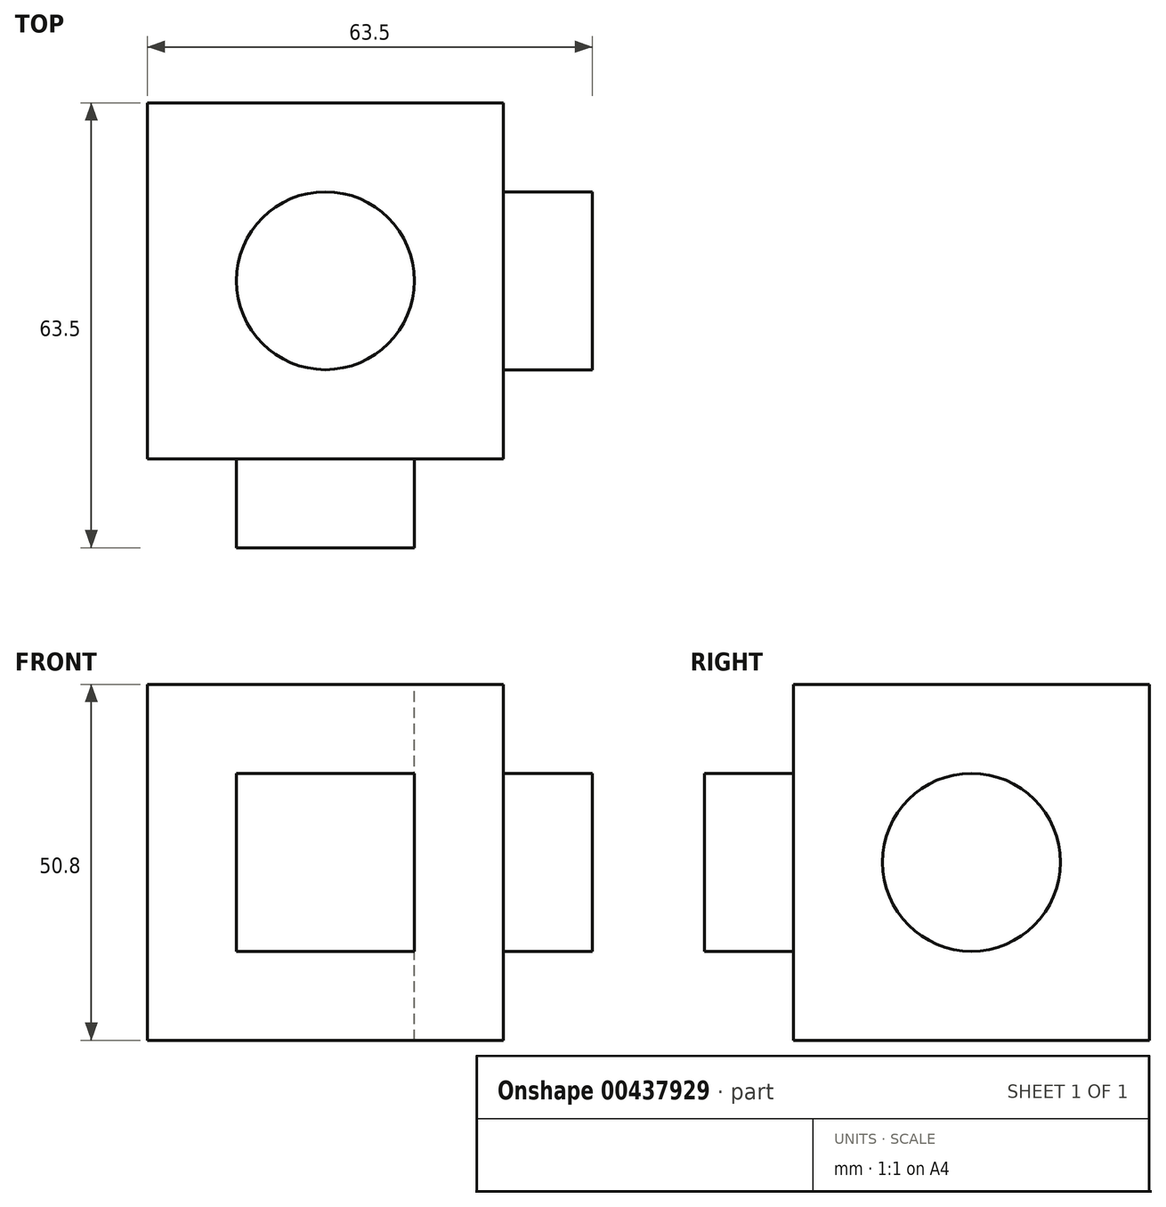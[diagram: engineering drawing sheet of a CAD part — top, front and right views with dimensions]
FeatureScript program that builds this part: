
annotation { "Feature Type Name" : "Feature", "Feature Type Description" : "" }
export const myFeature = defineFeature(function(context is Context, id is Id, definition is map)
    precondition{}
    {
        {
            var Q0;
            Q0=qCreatedBy(makeId("Front.planeOp"),FACE);
            var sketch = newSketch(context, id + "F0", { "sketchPlane" : qUnion([Q0])});
            skLineSegment(sketch, "E0", {"start": v(0, 0) * mm, "end": v(-50.8, 0) * mm});
            skLineSegment(sketch, "E1", {"start": v(-50.8, 0) * mm, "end": v(-50.8, 50.8) * mm});
            skLineSegment(sketch, "E2", {"start": v(-50.8, 50.8) * mm, "end": v(0, 50.8) * mm});
            skLineSegment(sketch, "E3", {"start": v(0, 50.8) * mm, "end": v(0, 0) * mm});
            skSolve(sketch);
        }
        {
            var Q0;
            Q0 = qSketchRegion(id + "F0", true);
            extrude(context, id + "F1", {"entities" : qUnion([Q0]), "depth" : 50.8 * mm});
        }
        {
            var Q0;
            Q0=makeQuery(id+"F1.opExtrude","CAP_FACE",FACE,{"disambiguationData":[OSD([sQuery(id+"F0.wireOp",EDGE,"E0"),sQuery(id+"F0.wireOp",EDGE,"E1"),sQuery(id+"F0.wireOp",EDGE,"E2"),sQuery(id+"F0.wireOp",EDGE,"E3")])],"isStart":false});
            var sketch = newSketch(context, id + "F2", { "sketchPlane" : qUnion([Q0])});
            skLineSegment(sketch, "E4.bottom", {"start": v(-38.1, 38.1) * mm, "end": v(-12.7, 38.1) * mm});
            skLineSegment(sketch, "E4.top", {"start": v(-38.1, 12.7) * mm, "end": v(-12.7, 12.7) * mm});
            skLineSegment(sketch, "E4.left", {"start": v(-38.1, 38.1) * mm, "end": v(-38.1, 12.7) * mm});
            skLineSegment(sketch, "E4.right", {"start": v(-12.7, 38.1) * mm, "end": v(-12.7, 12.7) * mm});
            skSolve(sketch);
        }
        {
            var Q0;
            Q0=makeQuery(id+"F2.imprint","IMPRINT",FACE,{"disambiguationData":[TD([[makeQuery(id+"F2.imprint","IMPRINT",EDGE,{"derivedFrom":sQuery(id+"F2.wireOp",EDGE,"E4.bottom")}),-1.0]])]});
            extrude(context, id + "F3", {"entities" : qUnion([Q0]), "operationType" : NewBodyOperationType.ADD, "depth" : 12.7 * mm});
        }
        {
            var Q0;
            Q0=makeQuery(id+"F1.opExtrude","SWEPT_FACE",FACE,{"disambiguationData":[OSD([sQuery(id+"F0.wireOp",EDGE,"E3")])]});
            var sketch = newSketch(context, id + "F4", { "sketchPlane" : qUnion([Q0])});
            skCircle(sketch, "E5", {"center": v(-25.4, 25.4) * mm, "radius": 12.7 * mm});
            skSolve(sketch);
        }
        {
            var Q0;
            Q0=makeQuery(id+"F4.imprint","IMPRINT",FACE,{"disambiguationData":[TD([[makeQuery(id+"F4.imprint","IMPRINT",EDGE,{"derivedFrom":sQuery(id+"F4.wireOp",EDGE,"E5")}),1.0]])]});
            extrude(context, id + "F5", {"entities" : qUnion([Q0]), "operationType" : NewBodyOperationType.ADD, "depth" : 12.7 * mm});
        }
        {
            var Q0;
            Q0=makeQuery(id+"F1.opExtrude","SWEPT_FACE",FACE,{"disambiguationData":[OSD([sQuery(id+"F0.wireOp",EDGE,"E2")])]});
            var sketch = newSketch(context, id + "F6", { "sketchPlane" : qUnion([Q0])});
            skCircle(sketch, "E6", {"center": v(-25.4, -25.4) * mm, "radius": 12.7 * mm});
            skSolve(sketch);
        }
        {
            var Q0;
            Q0=makeQuery(id+"F6.imprint","IMPRINT",FACE,{"disambiguationData":[TD([[makeQuery(id+"F6.imprint","IMPRINT",EDGE,{"derivedFrom":sQuery(id+"F6.wireOp",EDGE,"E6")}),1.0]])]});
            extrude(context, id + "F7", {"entities" : qUnion([Q0]), "operationType" : NewBodyOperationType.REMOVE, "oppositeDirection" : true, "depth" : 50.8 * mm});
        }
    });
